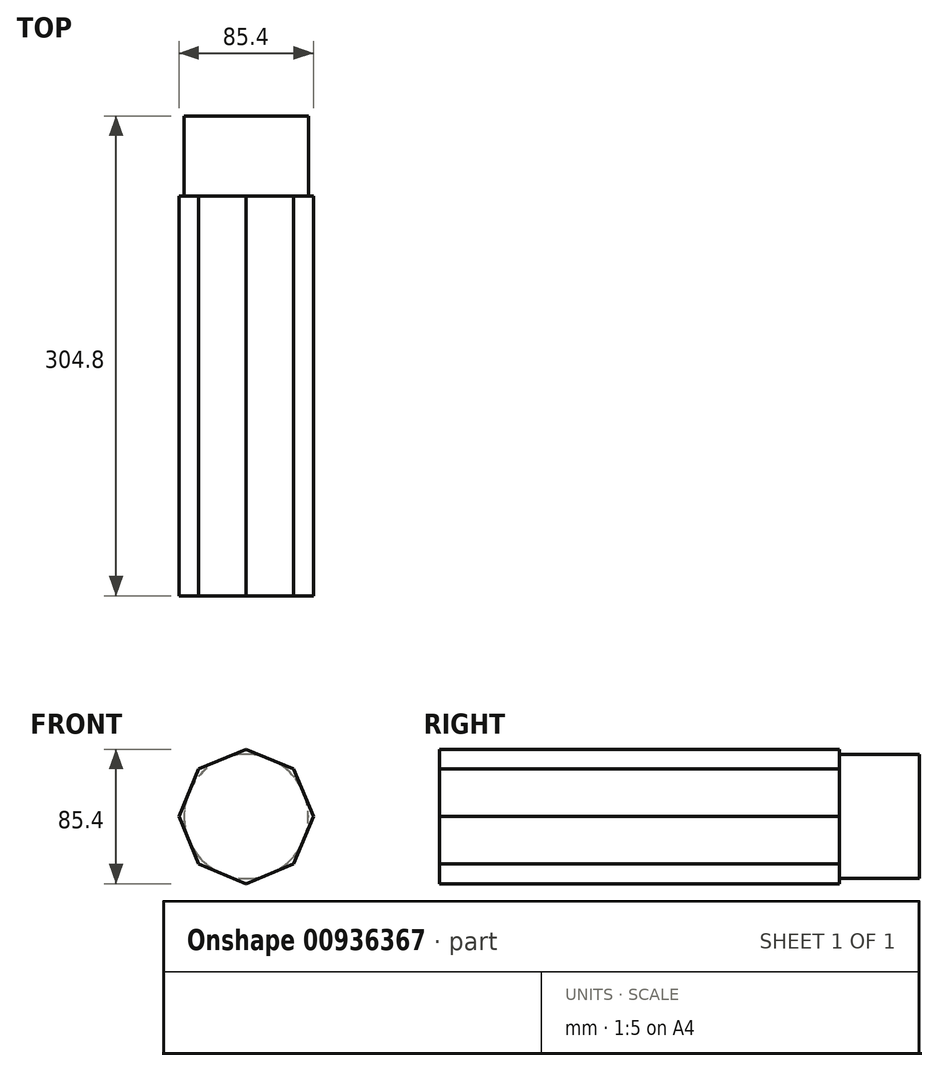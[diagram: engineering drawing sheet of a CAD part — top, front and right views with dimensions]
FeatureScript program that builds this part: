
annotation { "Feature Type Name" : "Feature", "Feature Type Description" : "" }
export const myFeature = defineFeature(function(context is Context, id is Id, definition is map)
    precondition{}
    {
        {
            var Q0;
            Q0=qCreatedBy(makeId("Front.planeOp"),FACE);
            var sketch = newSketch(context, id + "F0", { "sketchPlane" : qUnion([Q0])});
            skCircle(sketch, "E0", {"center": v(0, 0) * mm, "radius": 39.45 * mm});
            skSolve(sketch);
        }
        {
            var Q0;
            Q0=makeQuery(id+"F0.imprint","IMPRINT",FACE,{"disambiguationData":[TD([[makeQuery(id+"F0.imprint","IMPRINT",EDGE,{"derivedFrom":sQuery(id+"F0.wireOp",EDGE,"E0")}),1.0]])]});
            extrude(context, id + "F1", {"entities" : qUnion([Q0]), "endBound" : BoundingType.SYMMETRIC, "depth" : 50.8 * mm, "offsetDistance" : 25.4 * mm});
        }
        {
            var Q0;
            Q0=makeQuery(id+"F1.opExtrude","CAP_FACE",FACE,{"disambiguationData":[OSD([sQuery(id+"F0.wireOp",EDGE,"E0")])],"isStart":false});
            var sketch = newSketch(context, id + "F2", { "sketchPlane" : qUnion([Q0])});
            skCircle(sketch, "E1.cCircle", {"center": v(0, 0) * mm, "radius": 39.45 * mm, "construction": true});
            skLineSegment(sketch, "E1.0", {"start": v(30.2, -30.2) * mm, "end": v(0, -42.7) * mm});
            skLineSegment(sketch, "E1.1", {"start": v(0, -42.7) * mm, "end": v(-30.2, -30.2) * mm});
            skLineSegment(sketch, "E1.2", {"start": v(-30.2, -30.2) * mm, "end": v(-42.7, 0) * mm});
            skLineSegment(sketch, "E1.3", {"start": v(-42.7, 0) * mm, "end": v(-30.2, 30.2) * mm});
            skLineSegment(sketch, "E1.4", {"start": v(-30.2, 30.2) * mm, "end": v(0, 42.7) * mm});
            skLineSegment(sketch, "E1.5", {"start": v(0, 42.7) * mm, "end": v(30.2, 30.2) * mm});
            skLineSegment(sketch, "E1.6", {"start": v(30.2, 30.2) * mm, "end": v(42.7, 0) * mm});
            skLineSegment(sketch, "E1.7", {"start": v(42.7, 0) * mm, "end": v(30.2, -30.2) * mm});
            skPoint(sketch, "E1.0.midPoint", {"position": v(15.1, -36.45) * mm});
            skSolve(sketch);
        }
        {
            var Q0;
            {var subQ0=sQuery(id+"F2.wireOp",EDGE,"E1.7");var subQ1=sQuery(id+"F2.wireOp",EDGE,"E1.0");var subQ2=makeQuery(id+"F2.imprint","INTERSECT",VERTEX,{"derivedFrom":[subQ1,subQ0]});Q0=makeQuery(id+"F2.imprint","IMPRINT",FACE,{"disambiguationData":[TD([[makeQuery(id+"F2.imprint","IMPRINT",EDGE,{"disambiguationData":[TD([[subQ2,-1.0]])],"derivedFrom":subQ1}),-1.0]])]});}
            var Q1;
            {var subQ0=sQuery(id+"F2.wireOp",EDGE,"E1.1");var subQ1=sQuery(id+"F2.wireOp",EDGE,"E1.0");var subQ2=makeQuery(id+"F2.imprint","INTERSECT",VERTEX,{"derivedFrom":[subQ1,subQ0]});Q1=makeQuery(id+"F2.imprint","IMPRINT",FACE,{"disambiguationData":[TD([[makeQuery(id+"F2.imprint","IMPRINT",EDGE,{"disambiguationData":[TD([[subQ2,1.0]])],"derivedFrom":subQ1}),-1.0]])]});}
            var Q2;
            {var subQ0=sQuery(id+"F2.wireOp",EDGE,"E1.2");var subQ1=sQuery(id+"F2.wireOp",EDGE,"E1.1");var subQ2=makeQuery(id+"F2.imprint","INTERSECT",VERTEX,{"derivedFrom":[subQ1,subQ0]});Q2=makeQuery(id+"F2.imprint","IMPRINT",FACE,{"disambiguationData":[TD([[makeQuery(id+"F2.imprint","IMPRINT",EDGE,{"disambiguationData":[TD([[subQ2,1.0]])],"derivedFrom":subQ1}),-1.0]])]});}
            var Q3;
            {var subQ0=sQuery(id+"F2.wireOp",EDGE,"E1.3");var subQ1=sQuery(id+"F2.wireOp",EDGE,"E1.2");var subQ2=makeQuery(id+"F2.imprint","INTERSECT",VERTEX,{"derivedFrom":[subQ1,subQ0]});Q3=makeQuery(id+"F2.imprint","IMPRINT",FACE,{"disambiguationData":[TD([[makeQuery(id+"F2.imprint","IMPRINT",EDGE,{"disambiguationData":[TD([[subQ2,1.0]])],"derivedFrom":subQ1}),-1.0]])]});}
            var Q4;
            {var subQ0=sQuery(id+"F2.wireOp",EDGE,"E1.5");var subQ1=sQuery(id+"F2.wireOp",EDGE,"E1.4");var subQ2=makeQuery(id+"F2.imprint","INTERSECT",VERTEX,{"derivedFrom":[subQ1,subQ0]});Q4=makeQuery(id+"F2.imprint","IMPRINT",FACE,{"disambiguationData":[TD([[makeQuery(id+"F2.imprint","IMPRINT",EDGE,{"disambiguationData":[TD([[subQ2,1.0]])],"derivedFrom":subQ1}),-1.0]])]});}
            var Q5;
            {var subQ0=sQuery(id+"F2.wireOp",EDGE,"E1.6");var subQ1=sQuery(id+"F2.wireOp",EDGE,"E1.5");var subQ2=makeQuery(id+"F2.imprint","INTERSECT",VERTEX,{"derivedFrom":[subQ1,subQ0]});Q5=makeQuery(id+"F2.imprint","IMPRINT",FACE,{"disambiguationData":[TD([[makeQuery(id+"F2.imprint","IMPRINT",EDGE,{"disambiguationData":[TD([[subQ2,1.0]])],"derivedFrom":subQ1}),-1.0]])]});}
            var Q6;
            {var subQ0=sQuery(id+"F2.wireOp",EDGE,"E1.7");var subQ1=sQuery(id+"F2.wireOp",EDGE,"E1.6");var subQ2=makeQuery(id+"F2.imprint","INTERSECT",VERTEX,{"derivedFrom":[subQ1,subQ0]});Q6=makeQuery(id+"F2.imprint","IMPRINT",FACE,{"disambiguationData":[TD([[makeQuery(id+"F2.imprint","IMPRINT",EDGE,{"disambiguationData":[TD([[subQ2,1.0]])],"derivedFrom":subQ1}),-1.0]])]});}
            var Q7;
            {var subQ0=makeQuery(id+"F1.opExtrude","CAP_EDGE",EDGE,{"disambiguationData":[OSD([sQuery(id+"F0.wireOp",EDGE,"E0")])],"isStart":false});var subQ4=makeQuery(id+"F2.imprint","INTERSECT",VERTEX,{"derivedFrom":[subQ0,sQuery(id+"F2.wireOp",EDGE,"E1.0")]});Q7=makeQuery(id+"F2.imprint","IMPRINT",FACE,{"disambiguationData":[TD([[makeQuery(id+"F2.imprint","IMPRINT",EDGE,{"disambiguationData":[TD([[subQ4,1.0]])],"derivedFrom":subQ0}),1.0]])]});}
            var Q8;
            {var subQ0=sQuery(id+"F2.wireOp",EDGE,"E1.4");var subQ1=sQuery(id+"F2.wireOp",EDGE,"E1.3");var subQ2=makeQuery(id+"F2.imprint","INTERSECT",VERTEX,{"derivedFrom":[subQ1,subQ0]});Q8=makeQuery(id+"F2.imprint","IMPRINT",FACE,{"disambiguationData":[TD([[makeQuery(id+"F2.imprint","IMPRINT",EDGE,{"disambiguationData":[TD([[subQ2,1.0]])],"derivedFrom":subQ1}),-1.0]])]});}
            extrude(context, id + "F3", {"entities" : qUnion([Q0, Q1, Q2, Q3, Q4, Q5, Q6, Q7, Q8]), "operationType" : NewBodyOperationType.ADD, "depth" : 254 * mm, "offsetDistance" : 25.4 * mm});
        }
    });
